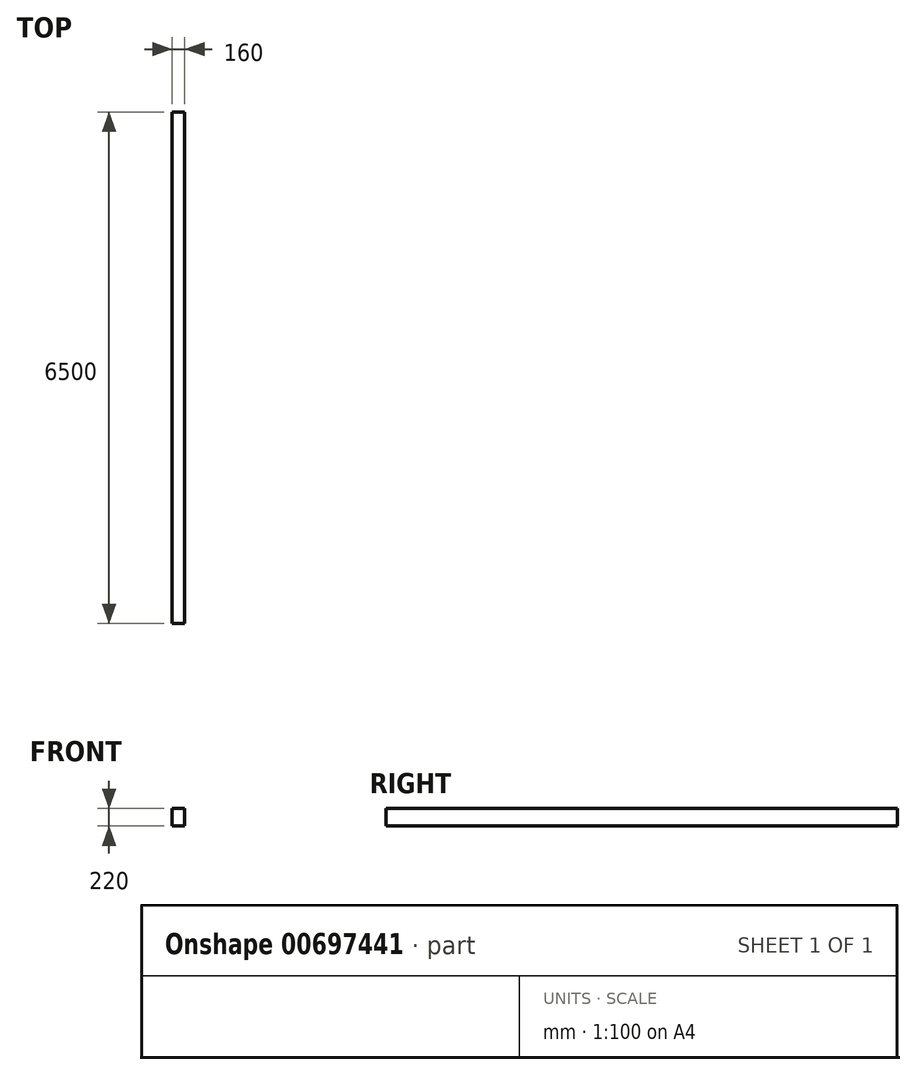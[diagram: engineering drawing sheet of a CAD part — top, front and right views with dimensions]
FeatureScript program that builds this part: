
annotation { "Feature Type Name" : "Feature", "Feature Type Description" : "" }
export const myFeature = defineFeature(function(context is Context, id is Id, definition is map)
    precondition{}
    {
        {
            var Q0;
            Q0=qCreatedBy(makeId("Front.planeOp"),FACE);
            var sketch = newSketch(context, id + "F0", { "sketchPlane" : qUnion([Q0])});
            skLineSegment(sketch, "E0.bottom", {"start": v(-109.75, -119.66) * mm, "end": v(50.25, -119.66) * mm});
            skLineSegment(sketch, "E0.top", {"start": v(-109.75, 100.34) * mm, "end": v(50.25, 100.34) * mm});
            skLineSegment(sketch, "E0.left", {"start": v(-109.75, -119.66) * mm, "end": v(-109.75, 100.34) * mm});
            skLineSegment(sketch, "E0.right", {"start": v(50.25, -119.66) * mm, "end": v(50.25, 100.34) * mm});
            skSolve(sketch);
        }
        {
            var Q0;
            Q0=makeQuery(id+"F0.imprint","IMPRINT",FACE,{"disambiguationData":[TD([[makeQuery(id+"F0.imprint","IMPRINT",EDGE,{"derivedFrom":sQuery(id+"F0.wireOp",EDGE,"E0.bottom")}),1.0]])]});
            extrude(context, id + "F1", {"entities" : qUnion([Q0]), "depth" : 6500 * mm, "offsetDistance" : 25 * mm});
        }
    });
